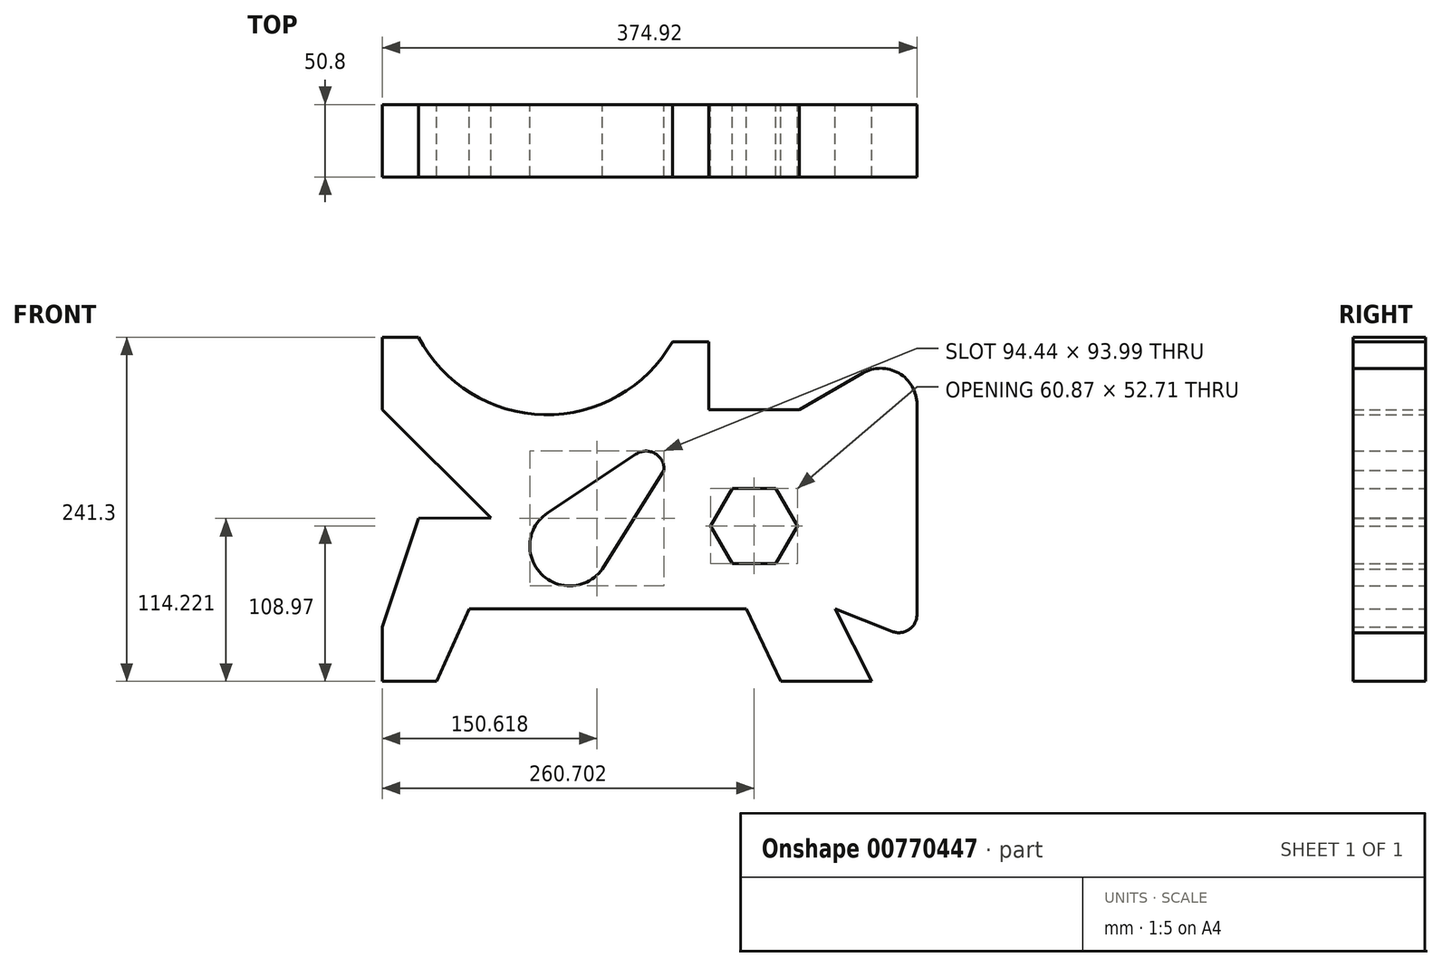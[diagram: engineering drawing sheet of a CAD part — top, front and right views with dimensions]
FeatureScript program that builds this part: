
annotation { "Feature Type Name" : "Feature", "Feature Type Description" : "" }
export const myFeature = defineFeature(function(context is Context, id is Id, definition is map)
    precondition{}
    {
        {
            var Q0;
            Q0=qCreatedBy(makeId("Front.planeOp"),FACE);
            var sketch = newSketch(context, id + "F0", { "sketchPlane" : qUnion([Q0])});
            skPoint(sketch, "E0.middle", {"position": v(-14.44, 185.9) * mm});
            skLineSegment(sketch, "E1", {"start": v(-44.92, 160.5) * mm, "end": v(-6.82, 160.5) * mm});
            skLineSegment(sketch, "E2", {"start": v(-6.82, 160.5) * mm, "end": v(16.04, 211.3) * mm});
            skLineSegment(sketch, "E3", {"start": v(16.04, 211.3) * mm, "end": v(210.52, 211.3) * mm});
            skLineSegment(sketch, "E4", {"start": v(210.52, 211.3) * mm, "end": v(234.48, 160.5) * mm});
            skLineSegment(sketch, "E5", {"start": v(234.48, 160.5) * mm, "end": v(298.3, 160.5) * mm});
            skLineSegment(sketch, "E6", {"start": v(298.3, 160.5) * mm, "end": v(272.58, 211.34) * mm});
            skLineSegment(sketch, "E7", {"start": v(330, 207.25) * mm, "end": v(330, 354.65) * mm});
            skLineSegment(sketch, "E8", {"start": v(272.58, 211.34) * mm, "end": v(312.62, 195.45) * mm});
            skPoint(sketch, "E9.newPointB", {"position": v(330, 114.01) * mm});
            skArc(sketch, "E9.filletArc", {"start": v(312.62, 195.45) * mm, "mid": v(324.44, 196.74) * mm, "end": v(330, 207.25) * mm});
            skLineSegment(sketch, "E10", {"start": v(-44.92, 160.5) * mm, "end": v(-44.92, 198.6) * mm});
            skLineSegment(sketch, "E11", {"start": v(-44.92, 198.6) * mm, "end": v(-19.48, 274.9) * mm});
            skLineSegment(sketch, "E12", {"start": v(-19.48, 274.9) * mm, "end": v(31.28, 275.09) * mm});
            skLineSegment(sketch, "E13", {"start": v(31.28, 275.09) * mm, "end": v(-44.92, 351) * mm});
            skLineSegment(sketch, "E14", {"start": v(-44.92, 351) * mm, "end": v(-44.92, 401.8) * mm});
            skLineSegment(sketch, "E15", {"start": v(-44.92, 401.8) * mm, "end": v(-19.52, 401.8) * mm});
            skLineSegment(sketch, "E16", {"start": v(184, 351) * mm, "end": v(184, 398.64) * mm});
            skLineSegment(sketch, "E17", {"start": v(184, 398.64) * mm, "end": v(158.6, 398.64) * mm});
            skArc(sketch, "E18", {"start": v(-19.52, 401.8) * mm, "mid": v(68.6, 347.5) * mm, "end": v(158.6, 398.64) * mm});
            skLineSegment(sketch, "E19", {"start": v(184, 351) * mm, "end": v(247.5, 351) * mm});
            skLineSegment(sketch, "E20", {"start": v(291.9, 376.64) * mm, "end": v(247.5, 351) * mm});
            skPoint(sketch, "E21.newPointA", {"position": v(330, 398.64) * mm});
            skPoint(sketch, "E21.newPointB", {"position": v(330, 393.29) * mm});
            skArc(sketch, "E21.filletArc", {"start": v(330, 354.65) * mm, "mid": v(317.3, 376.64) * mm, "end": v(291.9, 376.64) * mm});
            skLineSegment(sketch, "E22", {"start": v(132.98, 319.83) * mm, "end": v(71.02, 278.62) * mm});
            skLineSegment(sketch, "E23", {"start": v(152.7, 308.52) * mm, "end": v(109.39, 239.35) * mm});
            skArc(sketch, "E24", {"start": v(71.02, 278.62) * mm, "mid": v(66.5, 235.83) * mm, "end": v(109.39, 239.35) * mm});
            skArc(sketch, "E25", {"start": v(132.98, 319.83) * mm, "mid": v(146.34, 320.27) * mm, "end": v(152.7, 308.52) * mm});
            skLineSegment(sketch, "E26.0", {"start": v(231, 243.12) * mm, "end": v(200.56, 243.12) * mm});
            skLineSegment(sketch, "E26.1", {"start": v(200.56, 243.12) * mm, "end": v(185.35, 269.48) * mm});
            skLineSegment(sketch, "E26.2", {"start": v(185.35, 269.48) * mm, "end": v(200.56, 295.84) * mm});
            skLineSegment(sketch, "E26.3", {"start": v(200.56, 295.84) * mm, "end": v(231, 295.84) * mm});
            skLineSegment(sketch, "E26.4", {"start": v(231, 295.84) * mm, "end": v(246.22, 269.48) * mm});
            skLineSegment(sketch, "E26.5", {"start": v(246.22, 269.48) * mm, "end": v(231, 243.12) * mm});
            skPoint(sketch, "E26.0.midPoint", {"position": v(215.78, 243.12) * mm});
            skSolve(sketch);
        }
        {
            var Q0;
            Q0 = qSketchRegion(id + "F0", true);
            extrude(context, id + "F1", {"entities" : qUnion([Q0]), "endBound" : BoundingType.SYMMETRIC, "depth" : 50.8 * mm, "offsetDistance" : 25.4 * mm});
        }
    });
